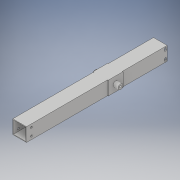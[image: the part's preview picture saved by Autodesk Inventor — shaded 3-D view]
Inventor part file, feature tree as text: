
AUTODESK INVENTOR PART (.ipt)
format: ipt  version: 2018 (Build 220112000, 112)  size: 194,560 bytes
history: native  units: in
note: dims shown in document units (in); Inventor stores cm internally (conversion verified against a paired STEP export)
features: extrude x6, sketch x6, other x1
ambient origin geometry x8: Origin, YZ Plane, XZ Plane, XY Plane, X Axis, Y Axis, Z Axis, Center Point
bodies: Solid1 (feature_tree)
feature tree (13):
  extrude  "Extrusion1"  Depth=5.25in
  extrude  "Extrusion2"  Depth=1.0in TaperAngle=0.0deg
  extrude  "Extrusion3"  Depth=0.5in TaperAngle=0.0deg
  extrude  "Extrusion4"  Depth=0.5in TaperAngle=0.0deg
  extrude  "Extrusion5"  Depth=6.0in
  extrude  "Extrusion6"  Depth=4.5in
  sketch  "Sketch1"  dims[d0=0.2in d1=5.25in]
  sketch  "Sketch2"  dims[d2=0.75in d3=1.0in d4=0.0in]
  sketch  "Sketch3"  dims[d5=0.5in d6=0.5in d7=0.0in]
  sketch  "Sketch4"  dims[d8=0.5in d9=0.5in d10=0.0in]
  sketch  "Sketch5"  dims[d11=4.5in d12=6.0in]
  sketch  "Sketch6"  dims[d13=0.0625in d14=0.0in d15=4.5in d16=6.0in d17=0.0625in d18=0.0in d19=0.0625in d20=0.0625in d21=0.0625in d22=0.0in]
  other  "Cut-Extrude3"
